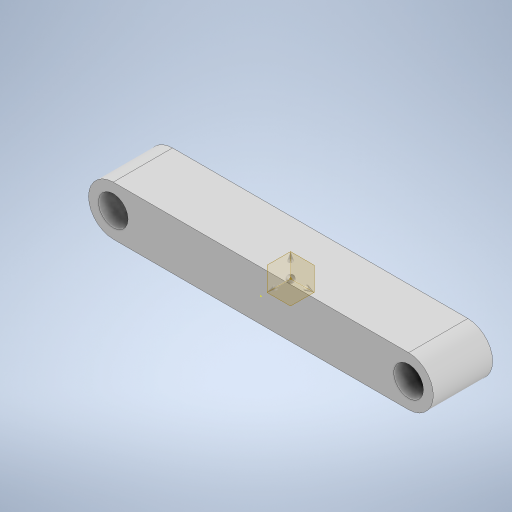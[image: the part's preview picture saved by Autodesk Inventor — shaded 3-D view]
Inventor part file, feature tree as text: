
AUTODESK INVENTOR PART (.ipt)
format: ipt  version: 2024 (Build 280153000, 153)  size: 236,032 bytes
history: native  units: mm
features: other x5, sketch x1
ambient origin geometry x8: Origin, YZ Plane, XZ Plane, XY Plane, X Axis, Y Axis, Z Axis, Center Point
bodies: Body1 (feature_tree)
feature tree (6):
  other  "PASADOR_1"
  other  "Generador_de_Piezas.ipt"
  other  "Desplazar cuerpo1"
  sketch  "Boceto1"  dims[d0=10.0mm d1=-687.735mm d2=-2406.905mm d3=0.0mm]
  other  "PASADOR_1::Generador_de_Piezas.ipt"
  other  "OperaciónIdentificador1"
